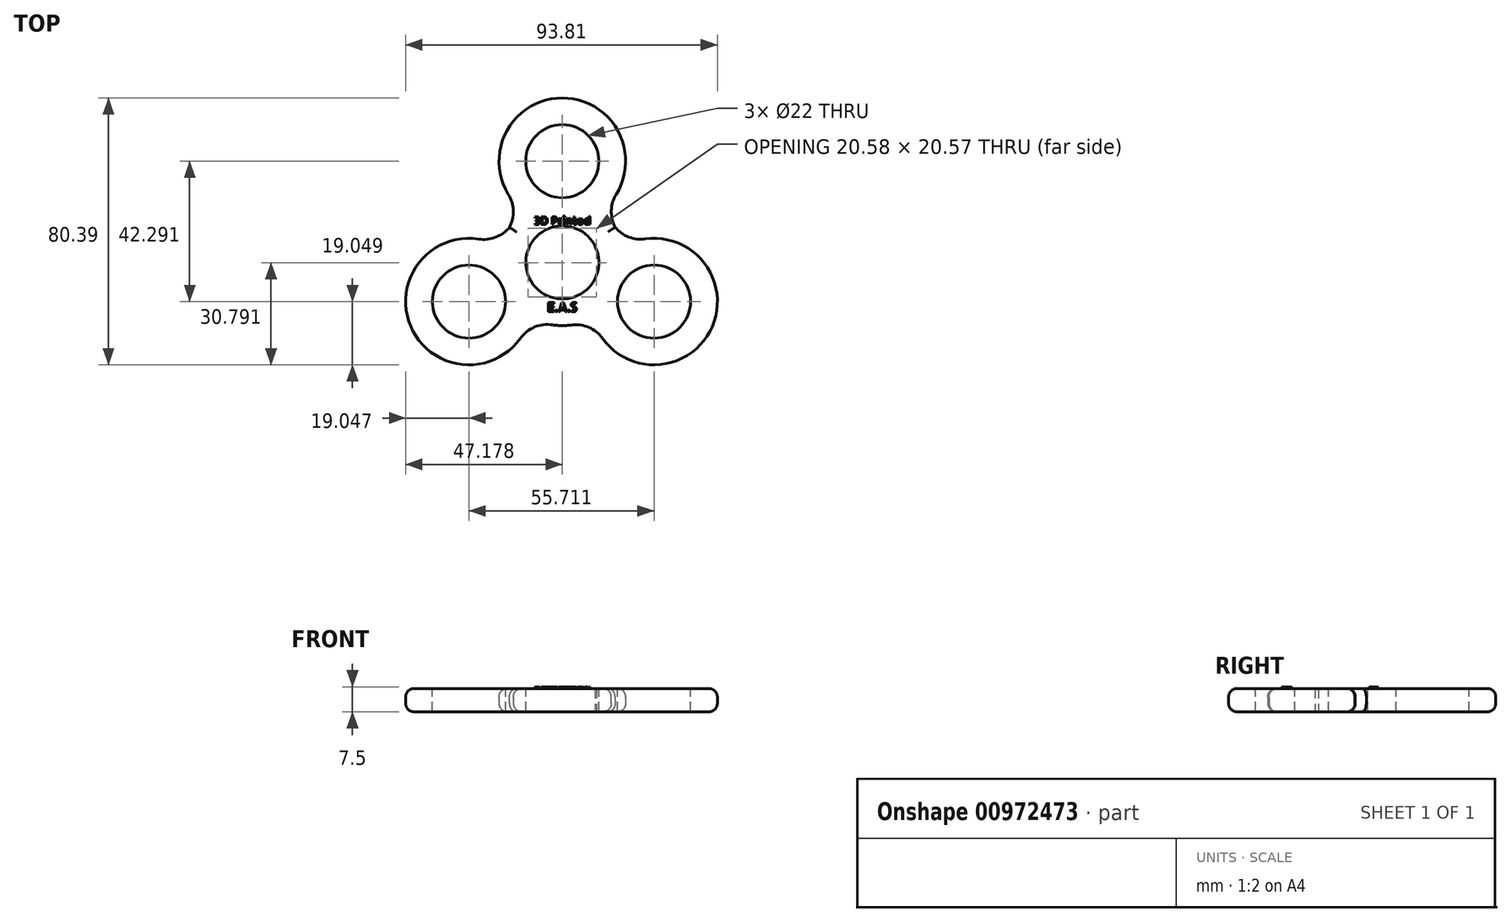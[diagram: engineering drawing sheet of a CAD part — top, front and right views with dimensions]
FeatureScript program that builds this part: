
annotation { "Feature Type Name" : "Feature", "Feature Type Description" : "" }
export const myFeature = defineFeature(function(context is Context, id is Id, definition is map)
    precondition{}
    {
        {
            var Q0;
            Q0=qCreatedBy(makeId("Top.planeOp"),FACE);
            var sketch = newSketch(context, id + "F0", { "sketchPlane" : qUnion([Q0])});
            skCircle(sketch, "E0", {"center": v(0, 0) * mm, "radius": 19.05 * mm});
            skSolve(sketch);
        }
        {
            var Q0;
            Q0=makeQuery(id+"F0.imprint","IMPRINT",FACE,{"disambiguationData":[TD([[makeQuery(id+"F0.imprint","IMPRINT",EDGE,{"derivedFrom":sQuery(id+"F0.wireOp",EDGE,"E0")}),1.0]])]});
            extrude(context, id + "F1", {"entities" : qUnion([Q0]), "depth" : 7 * mm, "offsetDistance" : 25.4 * mm});
        }
        {
            var Q0;
            Q0=makeQuery(id+"F1.opExtrude","CAP_FACE",FACE,{"disambiguationData":[OSD([sQuery(id+"F0.wireOp",EDGE,"E0")])],"isStart":false});
            var sketch = newSketch(context, id + "F2", { "sketchPlane" : qUnion([Q0])});
            skCircle(sketch, "E1", {"center": v(0, 0) * mm, "radius": 15.88 * mm});
            skSolve(sketch);
        }
        {
            var Q0;
            Q0=sQuery(id+"F2.wireOp",VERTEX,"E1.center");
            var Q1;
            Q1=makeQuery(id+"F1.opExtrude","SWEPT_BODY",BODY,{"disambiguationData":[OSD([sQuery(id+"F0.wireOp",EDGE,"E0")])]});
            hole(context, id + "F3", {"style" : HoleStyle.C_BORE, "endStyle" : HoleEndStyle.THROUGH, "holeDiameter" : 22 * mm, "cBoreDiameter" : 22 * mm, "cBoreDepth" : 6.35 * mm, "majorDiameter" : 6.35 * mm, "isTappedThrough" : true, "tappedDepth" : 12.7 * mm, "tapClearance" : 3, "locations" : qUnion([Q0]), "scope" : qUnion([Q1])});
        }
        {
            var Q0;
            Q0=qCreatedBy(makeId("Top.planeOp"),FACE);
            var sketch = newSketch(context, id + "F4", { "sketchPlane" : qUnion([Q0])});
            skCircle(sketch, "E2", {"center": v(0, 30.48) * mm, "radius": 19.05 * mm});
            skSolve(sketch);
        }
        {
            var Q0;
            Q0=makeQuery(id+"F4.imprint","IMPRINT",FACE,{"disambiguationData":[TD([[makeQuery(id+"F4.imprint","IMPRINT",EDGE,{"derivedFrom":sQuery(id+"F4.wireOp",EDGE,"E2")}),1.0]])]});
            extrude(context, id + "F5", {"entities" : qUnion([Q0]), "operationType" : NewBodyOperationType.ADD, "depth" : 7 * mm, "offsetDistance" : 25.4 * mm});
        }
        {
            var Q0;
            Q0=qCreatedBy(makeId("Top.planeOp"),FACE);
            var sketch = newSketch(context, id + "F6", { "sketchPlane" : qUnion([Q0])});
            skCircle(sketch, "E3", {"center": v(-28.1, -11.8) * mm, "radius": 19.05 * mm});
            skSolve(sketch);
        }
        {
            var Q0;
            Q0=makeQuery(id+"F6.imprint","IMPRINT",FACE,{"disambiguationData":[TD([[makeQuery(id+"F6.imprint","IMPRINT",EDGE,{"derivedFrom":sQuery(id+"F6.wireOp",EDGE,"E3")}),1.0]])]});
            extrude(context, id + "F7", {"entities" : qUnion([Q0]), "operationType" : NewBodyOperationType.ADD, "depth" : 7 * mm, "offsetDistance" : 25.4 * mm});
        }
        {
            var Q0;
            Q0=qCreatedBy(makeId("Top.planeOp"),FACE);
            var sketch = newSketch(context, id + "F8", { "sketchPlane" : qUnion([Q0])});
            skCircle(sketch, "E4", {"center": v(27.6, -11.81) * mm, "radius": 19.05 * mm});
            skSolve(sketch);
        }
        {
            var Q0;
            Q0=makeQuery(id+"F8.imprint","IMPRINT",FACE,{"disambiguationData":[TD([[makeQuery(id+"F8.imprint","IMPRINT",EDGE,{"derivedFrom":sQuery(id+"F8.wireOp",EDGE,"E4")}),1.0]])]});
            extrude(context, id + "F9", {"entities" : qUnion([Q0]), "operationType" : NewBodyOperationType.ADD, "depth" : 7 * mm, "offsetDistance" : 25.4 * mm});
        }
        {
            var Q0;
            Q0=makeQuery(id+"F9.boolean.opBoolean","MERGE",FACE,{"derivedFrom":[makeQuery(id+"F7.boolean.opBoolean","MERGE",FACE,{"derivedFrom":[makeQuery(id+"F5.boolean.opBoolean","MERGE",FACE,{"derivedFrom":[makeQuery(id+"F1.opExtrude","CAP_FACE",FACE,{"disambiguationData":[OSD([sQuery(id+"F0.wireOp",EDGE,"E0")])],"isStart":false}),makeQuery(id+"F5.opExtrude","CAP_FACE",FACE,{"disambiguationData":[OSD([sQuery(id+"F4.wireOp",EDGE,"E2")])],"isStart":false})]}),makeQuery(id+"F7.opExtrude","CAP_FACE",FACE,{"disambiguationData":[OSD([sQuery(id+"F6.wireOp",EDGE,"E3")])],"isStart":false})]}),makeQuery(id+"F9.opExtrude","CAP_FACE",FACE,{"disambiguationData":[OSD([sQuery(id+"F8.wireOp",EDGE,"E4")])],"isStart":false})]});
            var sketch = newSketch(context, id + "F10", { "sketchPlane" : qUnion([Q0])});
            skCircle(sketch, "E5", {"center": v(-28.1, -11.8) * mm, "radius": 11.3 * mm});
            skSolve(sketch);
        }
        {
            var Q0;
            Q0=sQuery(id+"F10.wireOp",VERTEX,"E5.center");
            var Q1;
            Q1=makeQuery(id+"F1.opExtrude","SWEPT_BODY",BODY,{"disambiguationData":[OSD([sQuery(id+"F0.wireOp",EDGE,"E0")])]});
            hole(context, id + "F11", {"style" : HoleStyle.C_BORE, "endStyle" : HoleEndStyle.THROUGH, "holeDiameter" : 22 * mm, "cBoreDiameter" : 22 * mm, "cBoreDepth" : 6.35 * mm, "majorDiameter" : 6.35 * mm, "isTappedThrough" : true, "tappedDepth" : 12.7 * mm, "tapClearance" : 3, "locations" : qUnion([Q0]), "scope" : qUnion([Q1])});
        }
        {
            var Q0;
            Q0=makeQuery(id+"F9.boolean.opBoolean","MERGE",FACE,{"derivedFrom":[makeQuery(id+"F7.boolean.opBoolean","MERGE",FACE,{"derivedFrom":[makeQuery(id+"F5.boolean.opBoolean","MERGE",FACE,{"derivedFrom":[makeQuery(id+"F1.opExtrude","CAP_FACE",FACE,{"disambiguationData":[OSD([sQuery(id+"F0.wireOp",EDGE,"E0")])],"isStart":false}),makeQuery(id+"F5.opExtrude","CAP_FACE",FACE,{"disambiguationData":[OSD([sQuery(id+"F4.wireOp",EDGE,"E2")])],"isStart":false})]}),makeQuery(id+"F7.opExtrude","CAP_FACE",FACE,{"disambiguationData":[OSD([sQuery(id+"F6.wireOp",EDGE,"E3")])],"isStart":false})]}),makeQuery(id+"F9.opExtrude","CAP_FACE",FACE,{"disambiguationData":[OSD([sQuery(id+"F8.wireOp",EDGE,"E4")])],"isStart":false})]});
            var sketch = newSketch(context, id + "F12", { "sketchPlane" : qUnion([Q0])});
            skCircle(sketch, "E6", {"center": v(27.6, -11.81) * mm, "radius": 11.3 * mm});
            skSolve(sketch);
        }
        {
            var Q0;
            Q0=sQuery(id+"F12.wireOp",VERTEX,"E6.center");
            var Q1;
            Q1=makeQuery(id+"F1.opExtrude","SWEPT_BODY",BODY,{"disambiguationData":[OSD([sQuery(id+"F0.wireOp",EDGE,"E0")])]});
            hole(context, id + "F13", {"style" : HoleStyle.C_BORE, "endStyle" : HoleEndStyle.THROUGH, "holeDiameter" : 22 * mm, "cBoreDiameter" : 22 * mm, "cBoreDepth" : 6.35 * mm, "majorDiameter" : 6.35 * mm, "isTappedThrough" : true, "tappedDepth" : 12.7 * mm, "tapClearance" : 3, "locations" : qUnion([Q0]), "scope" : qUnion([Q1])});
        }
        {
            var Q0;
            Q0=makeQuery(id+"F9.boolean.opBoolean","MERGE",FACE,{"derivedFrom":[makeQuery(id+"F7.boolean.opBoolean","MERGE",FACE,{"derivedFrom":[makeQuery(id+"F5.boolean.opBoolean","MERGE",FACE,{"derivedFrom":[makeQuery(id+"F1.opExtrude","CAP_FACE",FACE,{"disambiguationData":[OSD([sQuery(id+"F0.wireOp",EDGE,"E0")])],"isStart":false}),makeQuery(id+"F5.opExtrude","CAP_FACE",FACE,{"disambiguationData":[OSD([sQuery(id+"F4.wireOp",EDGE,"E2")])],"isStart":false})]}),makeQuery(id+"F7.opExtrude","CAP_FACE",FACE,{"disambiguationData":[OSD([sQuery(id+"F6.wireOp",EDGE,"E3")])],"isStart":false})]}),makeQuery(id+"F9.opExtrude","CAP_FACE",FACE,{"disambiguationData":[OSD([sQuery(id+"F8.wireOp",EDGE,"E4")])],"isStart":false})]});
            var sketch = newSketch(context, id + "F14", { "sketchPlane" : qUnion([Q0])});
            skCircle(sketch, "E7", {"center": v(0, 30.48) * mm, "radius": 15.36 * mm});
            skSolve(sketch);
        }
        {
            var Q0;
            Q0=sQuery(id+"F14.wireOp",VERTEX,"E7.center");
            var Q1;
            Q1=makeQuery(id+"F1.opExtrude","SWEPT_BODY",BODY,{"disambiguationData":[OSD([sQuery(id+"F0.wireOp",EDGE,"E0")])]});
            hole(context, id + "F15", {"style" : HoleStyle.C_BORE, "endStyle" : HoleEndStyle.THROUGH, "holeDiameter" : 22 * mm, "cBoreDiameter" : 22 * mm, "cBoreDepth" : 6.35 * mm, "majorDiameter" : 6.35 * mm, "isTappedThrough" : true, "tappedDepth" : 12.7 * mm, "tapClearance" : 3, "locations" : qUnion([Q0]), "scope" : qUnion([Q1])});
        }
        {
            var Q0;
            Q0=makeQuery(id+"FhpWLzmgRi7eI2M_1.opFillet","SPLIT",FACE,{"disambiguationData":[OD(0.0)],"derivedFrom":makeQuery(id+"F9.boolean.opBoolean","MERGE",FACE,{"derivedFrom":[makeQuery(id+"F7.boolean.opBoolean","MERGE",FACE,{"derivedFrom":[makeQuery(id+"F5.boolean.opBoolean","MERGE",FACE,{"derivedFrom":[makeQuery(id+"F1.opExtrude","CAP_FACE",FACE,{"disambiguationData":[OSD([sQuery(id+"F0.wireOp",EDGE,"E0")])],"isStart":false}),makeQuery(id+"F5.opExtrude","CAP_FACE",FACE,{"disambiguationData":[OSD([sQuery(id+"F4.wireOp",EDGE,"E2")])],"isStart":false})]}),makeQuery(id+"F7.opExtrude","CAP_FACE",FACE,{"disambiguationData":[OSD([sQuery(id+"F6.wireOp",EDGE,"E3")])],"isStart":false})]}),makeQuery(id+"F9.opExtrude","CAP_FACE",FACE,{"disambiguationData":[OSD([sQuery(id+"F8.wireOp",EDGE,"E4")])],"isStart":false})]})});
            var sketch = newSketch(context, id + "F16", { "sketchPlane" : qUnion([Q0])});
            skText(sketch, "E8", { "text": "3D Printed", "fontName": "AllertaStencil-Regular.ttf"});
            const initialGuessF16  = {"E8": [-0.00853, 0.01137, 1, 0, 0.00237]};
            skSetInitialGuess(sketch, initialGuessF16);
            skSolve(sketch);
        }
        {
            var Q0;
            Q0 = qSketchRegion(id + "F16", true);
            extrude(context, id + "F17", {"entities" : qUnion([Q0]), "operationType" : NewBodyOperationType.ADD, "depth" : 0.5 * mm, "offsetDistance" : 25.4 * mm});
        }
        {
            var Q0;
            Q0=makeQuery(id+"FhpWLzmgRi7eI2M_1.opFillet","SPLIT",FACE,{"disambiguationData":[OD(0.0)],"derivedFrom":makeQuery(id+"F9.boolean.opBoolean","MERGE",FACE,{"derivedFrom":[makeQuery(id+"F7.boolean.opBoolean","MERGE",FACE,{"derivedFrom":[makeQuery(id+"F5.boolean.opBoolean","MERGE",FACE,{"derivedFrom":[makeQuery(id+"F1.opExtrude","CAP_FACE",FACE,{"disambiguationData":[OSD([sQuery(id+"F0.wireOp",EDGE,"E0")])],"isStart":false}),makeQuery(id+"F5.opExtrude","CAP_FACE",FACE,{"disambiguationData":[OSD([sQuery(id+"F4.wireOp",EDGE,"E2")])],"isStart":false})]}),makeQuery(id+"F7.opExtrude","CAP_FACE",FACE,{"disambiguationData":[OSD([sQuery(id+"F6.wireOp",EDGE,"E3")])],"isStart":false})]}),makeQuery(id+"F9.opExtrude","CAP_FACE",FACE,{"disambiguationData":[OSD([sQuery(id+"F8.wireOp",EDGE,"E4")])],"isStart":false})]})});
            var sketch = newSketch(context, id + "F18", { "sketchPlane" : qUnion([Q0])});
            skText(sketch, "E9", { "text": "E.A.S", "fontName": "AllertaStencil-Regular.ttf"});
            const initialGuessF18  = {"E9": [-0.00454, -0.01489, 1, 0, 0.00282]};
            skSetInitialGuess(sketch, initialGuessF18);
            skSolve(sketch);
        }
        {
            var Q0;
            Q0 = qSketchRegion(id + "F18", true);
            extrude(context, id + "F19", {"entities" : qUnion([Q0]), "operationType" : NewBodyOperationType.ADD, "depth" : 0.5 * mm, "offsetDistance" : 25.4 * mm});
        }
        {
            var Q0;
            Q0=makeQuery(id+"F7.boolean.opBoolean","INTERSECT",EDGE,{"disambiguationData":[OD(0.0)],"derivedFrom":[makeQuery(id+"F1.opExtrude","SWEPT_FACE",FACE,{"disambiguationData":[OSD([sQuery(id+"F0.wireOp",EDGE,"E0")])]}),makeQuery(id+"F7.opExtrude","SWEPT_FACE",FACE,{"disambiguationData":[OSD([sQuery(id+"F6.wireOp",EDGE,"E3")])]})]});
            var Q1;
            Q1=makeQuery(id+"F7.boolean.opBoolean","INTERSECT",EDGE,{"disambiguationData":[OD(1.0)],"derivedFrom":[makeQuery(id+"F1.opExtrude","SWEPT_FACE",FACE,{"disambiguationData":[OSD([sQuery(id+"F0.wireOp",EDGE,"E0")])]}),makeQuery(id+"F7.opExtrude","SWEPT_FACE",FACE,{"disambiguationData":[OSD([sQuery(id+"F6.wireOp",EDGE,"E3")])]})]});
            var Q2;
            Q2=makeQuery(id+"F9.boolean.opBoolean","INTERSECT",EDGE,{"disambiguationData":[OD(1.0)],"derivedFrom":[makeQuery(id+"F7.boolean.opBoolean","SPLIT",FACE,{"disambiguationData":[OD(1.0)],"derivedFrom":makeQuery(id+"F1.opExtrude","SWEPT_FACE",FACE,{"disambiguationData":[OSD([sQuery(id+"F0.wireOp",EDGE,"E0")])]})}),makeQuery(id+"F9.opExtrude","SWEPT_FACE",FACE,{"disambiguationData":[OSD([sQuery(id+"F8.wireOp",EDGE,"E4")])]})]});
            var Q3;
            Q3=makeQuery(id+"F9.boolean.opBoolean","INTERSECT",EDGE,{"disambiguationData":[OD(0.0)],"derivedFrom":[makeQuery(id+"F7.boolean.opBoolean","SPLIT",FACE,{"disambiguationData":[OD(1.0)],"derivedFrom":makeQuery(id+"F1.opExtrude","SWEPT_FACE",FACE,{"disambiguationData":[OSD([sQuery(id+"F0.wireOp",EDGE,"E0")])]})}),makeQuery(id+"F9.opExtrude","SWEPT_FACE",FACE,{"disambiguationData":[OSD([sQuery(id+"F8.wireOp",EDGE,"E4")])]})]});
            var Q4;
            Q4=makeQuery(id+"F5.boolean.opBoolean","INTERSECT",EDGE,{"disambiguationData":[OD(1.0)],"derivedFrom":[makeQuery(id+"F1.opExtrude","SWEPT_FACE",FACE,{"disambiguationData":[OSD([sQuery(id+"F0.wireOp",EDGE,"E0")])]}),makeQuery(id+"F5.opExtrude","SWEPT_FACE",FACE,{"disambiguationData":[OSD([sQuery(id+"F4.wireOp",EDGE,"E2")])]})]});
            var Q5;
            Q5=makeQuery(id+"F5.boolean.opBoolean","INTERSECT",EDGE,{"disambiguationData":[OD(0.0)],"derivedFrom":[makeQuery(id+"F1.opExtrude","SWEPT_FACE",FACE,{"disambiguationData":[OSD([sQuery(id+"F0.wireOp",EDGE,"E0")])]}),makeQuery(id+"F5.opExtrude","SWEPT_FACE",FACE,{"disambiguationData":[OSD([sQuery(id+"F4.wireOp",EDGE,"E2")])]})]});
            fillet(context, id + "F20", {"entities" : qUnion([Q0, Q1, Q2, Q3, Q4, Q5]), "radius" : 10 * mm, "tangentPropagation" : true, "allowEdgeOverflow" : false});
        }
        {
            var Q0;
            Q0=makeQuery(id+"F5.opExtrude","CAP_EDGE",EDGE,{"disambiguationData":[OSD([sQuery(id+"F4.wireOp",EDGE,"E2")])],"isStart":false});
            var Q1;
            {var subQ0=sQuery(id+"F4.wireOp",EDGE,"E2");var subQ1=sQuery(id+"F0.wireOp",EDGE,"E0");Q1=makeQuery(id+"F20.opFillet","BLEND_EDGE",EDGE,{"blendedFrom":[makeQuery(id+"F5.boolean.opBoolean","INTERSECT",EDGE,{"disambiguationData":[OD(0.0)],"derivedFrom":[makeQuery(id+"F1.opExtrude","SWEPT_FACE",FACE,{"disambiguationData":[OSD([subQ1])]}),makeQuery(id+"F5.opExtrude","SWEPT_FACE",FACE,{"disambiguationData":[OSD([subQ0])]})]}),makeQuery(id+"F9.boolean.opBoolean","MERGE",FACE,{"derivedFrom":[makeQuery(id+"F7.boolean.opBoolean","MERGE",FACE,{"derivedFrom":[makeQuery(id+"F5.boolean.opBoolean","MERGE",FACE,{"derivedFrom":[makeQuery(id+"F1.opExtrude","CAP_FACE",FACE,{"disambiguationData":[OSD([subQ1])],"isStart":false}),makeQuery(id+"F5.opExtrude","CAP_FACE",FACE,{"disambiguationData":[OSD([subQ0])],"isStart":false})]}),makeQuery(id+"F7.opExtrude","CAP_FACE",FACE,{"disambiguationData":[OSD([sQuery(id+"F6.wireOp",EDGE,"E3")])],"isStart":false})]}),makeQuery(id+"F9.opExtrude","CAP_FACE",FACE,{"disambiguationData":[OSD([sQuery(id+"F8.wireOp",EDGE,"E4")])],"isStart":false})]})],"blendedInto":[makeQuery(id+"F9.boolean.opBoolean","MERGE",FACE,{"derivedFrom":[makeQuery(id+"F7.boolean.opBoolean","MERGE",FACE,{"derivedFrom":[makeQuery(id+"F5.boolean.opBoolean","MERGE",FACE,{"derivedFrom":[makeQuery(id+"F1.opExtrude","CAP_FACE",FACE,{"disambiguationData":[OSD([subQ1])],"isStart":false}),makeQuery(id+"F5.opExtrude","CAP_FACE",FACE,{"disambiguationData":[OSD([subQ0])],"isStart":false})]}),makeQuery(id+"F7.opExtrude","CAP_FACE",FACE,{"disambiguationData":[OSD([sQuery(id+"F6.wireOp",EDGE,"E3")])],"isStart":false})]}),makeQuery(id+"F9.opExtrude","CAP_FACE",FACE,{"disambiguationData":[OSD([sQuery(id+"F8.wireOp",EDGE,"E4")])],"isStart":false})]})]});}
            var Q2;
            {var subQ0=sQuery(id+"F6.wireOp",EDGE,"E3");var subQ1=sQuery(id+"F0.wireOp",EDGE,"E0");Q2=makeQuery(id+"F20.opFillet","BLEND_EDGE",EDGE,{"blendedFrom":[makeQuery(id+"F7.boolean.opBoolean","INTERSECT",EDGE,{"disambiguationData":[OD(0.0)],"derivedFrom":[makeQuery(id+"F1.opExtrude","SWEPT_FACE",FACE,{"disambiguationData":[OSD([subQ1])]}),makeQuery(id+"F7.opExtrude","SWEPT_FACE",FACE,{"disambiguationData":[OSD([subQ0])]})]}),makeQuery(id+"F9.boolean.opBoolean","MERGE",FACE,{"derivedFrom":[makeQuery(id+"F7.boolean.opBoolean","MERGE",FACE,{"derivedFrom":[makeQuery(id+"F5.boolean.opBoolean","MERGE",FACE,{"derivedFrom":[makeQuery(id+"F1.opExtrude","CAP_FACE",FACE,{"disambiguationData":[OSD([subQ1])],"isStart":false}),makeQuery(id+"F5.opExtrude","CAP_FACE",FACE,{"disambiguationData":[OSD([sQuery(id+"F4.wireOp",EDGE,"E2")])],"isStart":false})]}),makeQuery(id+"F7.opExtrude","CAP_FACE",FACE,{"disambiguationData":[OSD([subQ0])],"isStart":false})]}),makeQuery(id+"F9.opExtrude","CAP_FACE",FACE,{"disambiguationData":[OSD([sQuery(id+"F8.wireOp",EDGE,"E4")])],"isStart":false})]})],"blendedInto":[makeQuery(id+"F9.boolean.opBoolean","MERGE",FACE,{"derivedFrom":[makeQuery(id+"F7.boolean.opBoolean","MERGE",FACE,{"derivedFrom":[makeQuery(id+"F5.boolean.opBoolean","MERGE",FACE,{"derivedFrom":[makeQuery(id+"F1.opExtrude","CAP_FACE",FACE,{"disambiguationData":[OSD([subQ1])],"isStart":false}),makeQuery(id+"F5.opExtrude","CAP_FACE",FACE,{"disambiguationData":[OSD([sQuery(id+"F4.wireOp",EDGE,"E2")])],"isStart":false})]}),makeQuery(id+"F7.opExtrude","CAP_FACE",FACE,{"disambiguationData":[OSD([subQ0])],"isStart":false})]}),makeQuery(id+"F9.opExtrude","CAP_FACE",FACE,{"disambiguationData":[OSD([sQuery(id+"F8.wireOp",EDGE,"E4")])],"isStart":false})]})]});}
            var Q3;
            Q3=makeQuery(id+"F5.opExtrude","CAP_EDGE",EDGE,{"disambiguationData":[OSD([sQuery(id+"F4.wireOp",EDGE,"E2")])],"isStart":true});
            var Q4;
            Q4=makeQuery(id+"F7.opExtrude","CAP_EDGE",EDGE,{"disambiguationData":[OSD([sQuery(id+"F6.wireOp",EDGE,"E3")])],"isStart":true});
            fillet(context, id + "F21", {"entities" : qUnion([Q0, Q1, Q2, Q3, Q4]), "radius" : 2.5 * mm, "tangentPropagation" : true, "allowEdgeOverflow" : false});
        }
    });
